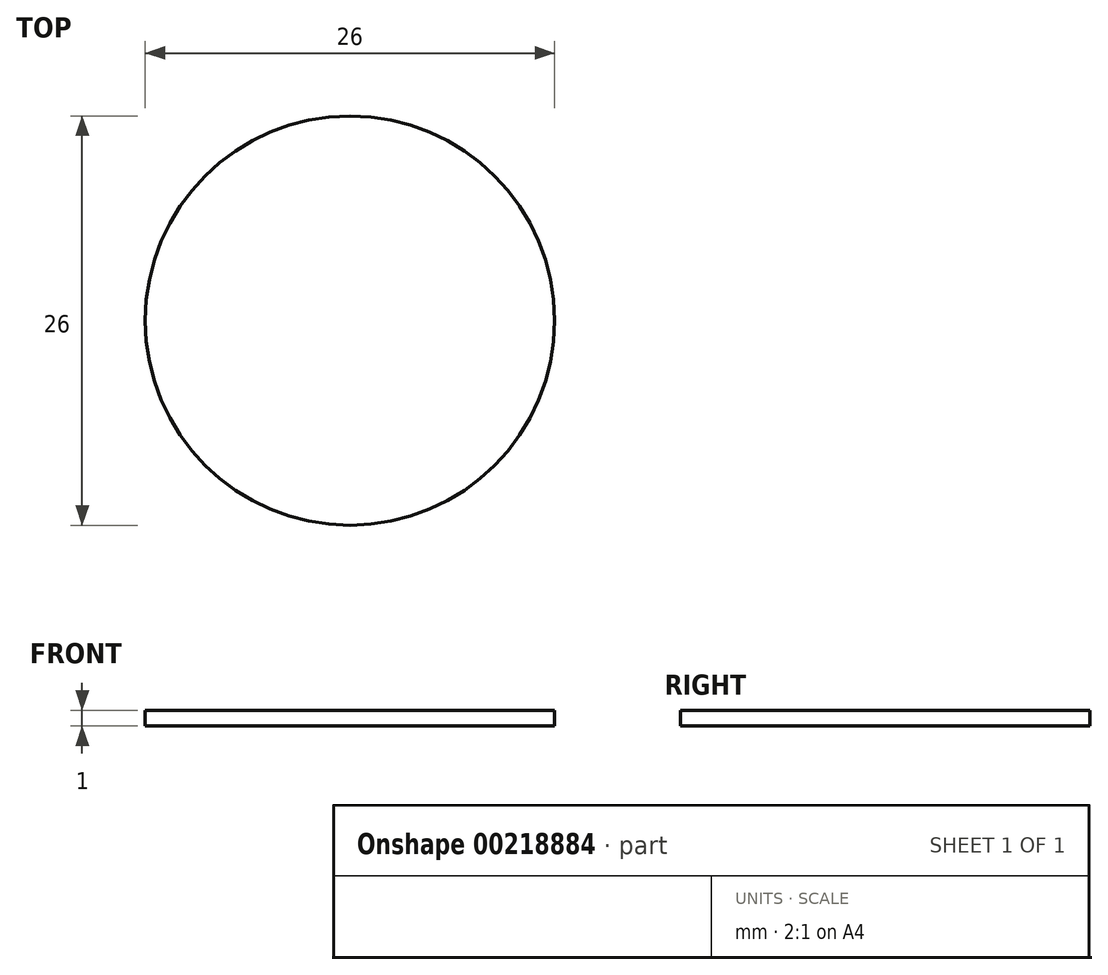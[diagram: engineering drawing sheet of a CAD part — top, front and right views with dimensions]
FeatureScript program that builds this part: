
annotation { "Feature Type Name" : "Feature", "Feature Type Description" : "" }
export const myFeature = defineFeature(function(context is Context, id is Id, definition is map)
    precondition{}
    {
        {
            var Q0;
            Q0=qCreatedBy(makeId("Top.planeOp"),FACE);
            var sketch = newSketch(context, id + "F0", { "sketchPlane" : qUnion([Q0])});
            skCircle(sketch, "E0", {"center": v(0, 0) * mm, "radius": 13 * mm});
            skSolve(sketch);
        }
        {
            var Q0;
            Q0 = qSketchRegion(id + "F0", true);
            extrude(context, id + "F1", {"entities" : qUnion([Q0]), "depth" : 1 * mm});
        }
    });
